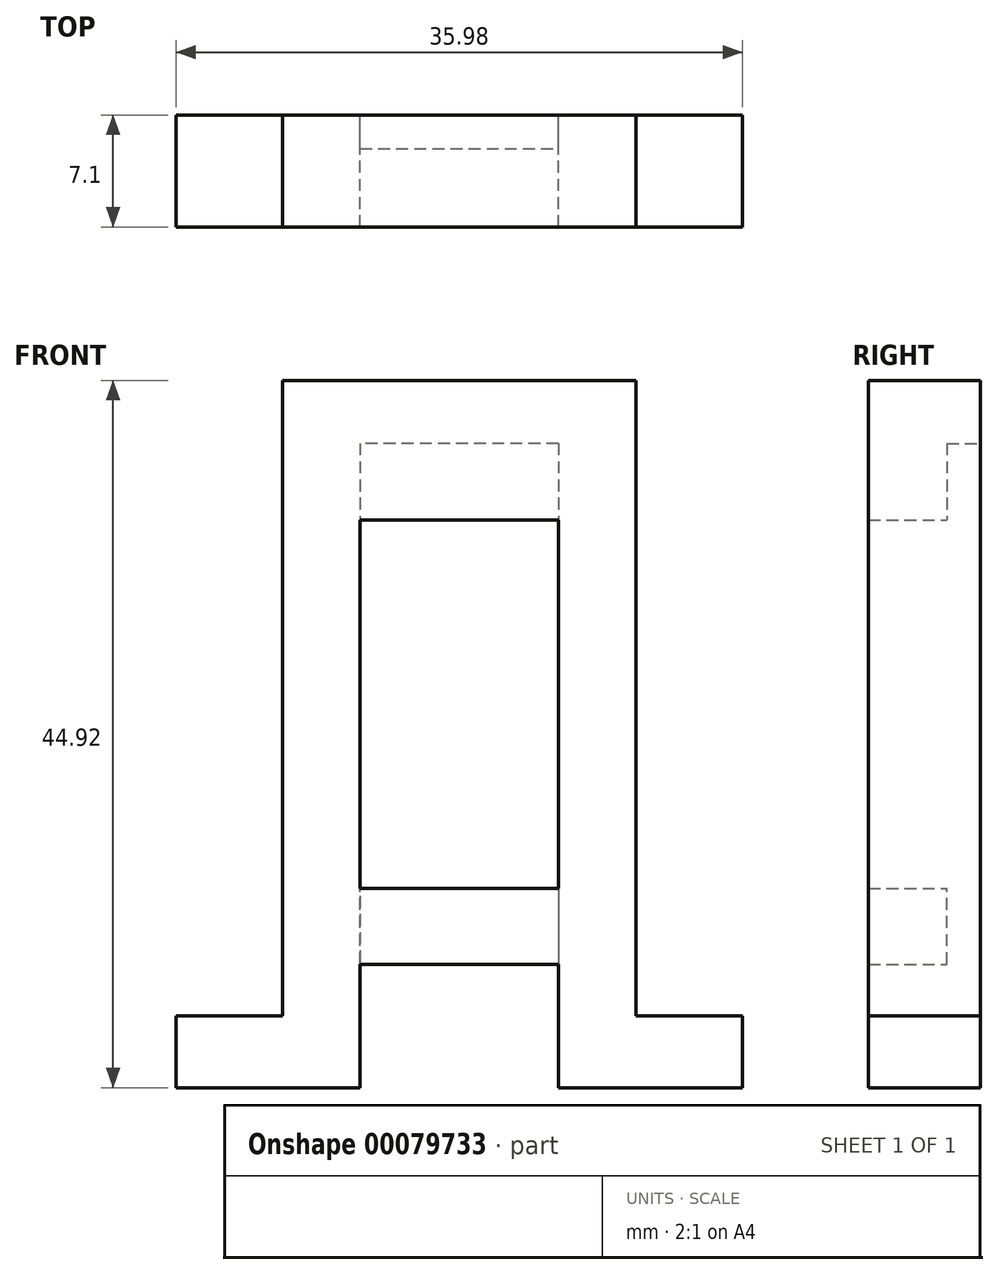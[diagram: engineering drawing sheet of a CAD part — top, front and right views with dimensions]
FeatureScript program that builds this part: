
annotation { "Feature Type Name" : "Feature", "Feature Type Description" : "" }
export const myFeature = defineFeature(function(context is Context, id is Id, definition is map)
    precondition{}
    {
        {
            var Q0;
            Q0=qCreatedBy(makeId("Front.planeOp"),FACE);
            var sketch = newSketch(context, id + "F0", { "sketchPlane" : qUnion([Q0])});
            skLineSegment(sketch, "E0.bottom", {"start": v(-11.23, 22.46) * mm, "end": v(11.23, 22.46) * mm});
            skLineSegment(sketch, "E0.top", {"start": v(-18, -22.46) * mm, "end": v(-6.3, -22.46) * mm});
            skLineSegment(sketch, "E0.left", {"start": v(-17.99, -17.91) * mm, "end": v(-17.99, -22.46) * mm});
            skLineSegment(sketch, "E0.right", {"start": v(17.99, -17.91) * mm, "end": v(17.99, -22.46) * mm});
            skPoint(sketch, "E0.middle", {"position": v(0, 0) * mm});
            skLineSegment(sketch, "E1", {"start": v(-18, -22.46) * mm, "end": v(-18, -17.91) * mm, "construction": true});
            skLineSegment(sketch, "E2", {"start": v(-18, -17.91) * mm, "end": v(-11.23, -17.91) * mm, "construction": true});
            skLineSegment(sketch, "E3", {"start": v(-18, -22.46) * mm, "end": v(-6.3, -22.46) * mm, "construction": true});
            skLineSegment(sketch, "E4", {"start": v(17.99, -22.46) * mm, "end": v(6.3, -22.46) * mm, "construction": true});
            skLineSegment(sketch, "E5", {"start": v(-6.3, -22.46) * mm, "end": v(-6.3, -14.62) * mm, "construction": true});
            skLineSegment(sketch, "E6", {"start": v(6.3, -22.46) * mm, "end": v(6.3, -14.62) * mm, "construction": true});
            skLineSegment(sketch, "E7", {"start": v(-6.3, 13.58) * mm, "end": v(6.3, 13.58) * mm, "construction": true});
            skLineSegment(sketch, "E8.trimOffspring", {"start": v(11.23, -17.91) * mm, "end": v(17.99, -17.91) * mm, "construction": true});
            skLineSegment(sketch, "E9", {"start": v(-6.3, 13.58) * mm, "end": v(-6.3, -9.82) * mm});
            skLineSegment(sketch, "E10", {"start": v(-6.3, 13.58) * mm, "end": v(6.3, 13.58) * mm});
            skLineSegment(sketch, "E11", {"start": v(-6.3, -9.82) * mm, "end": v(6.3, -9.82) * mm});
            skLineSegment(sketch, "E12", {"start": v(6.3, -9.82) * mm, "end": v(6.3, 13.58) * mm});
            skLineSegment(sketch, "E13", {"start": v(-6.3, -14.62) * mm, "end": v(6.3, -14.62) * mm});
            skLineSegment(sketch, "E14", {"start": v(6.3, -14.62) * mm, "end": v(6.3, -22.46) * mm});
            skLineSegment(sketch, "E15", {"start": v(-6.3, -14.62) * mm, "end": v(-6.3, -22.46) * mm});
            skLineSegment(sketch, "E16", {"start": v(-6.3, 22.46) * mm, "end": v(-11.23, 22.46) * mm, "construction": true});
            skLineSegment(sketch, "E17", {"start": v(6.3, 22.46) * mm, "end": v(11.23, 22.46) * mm, "construction": true});
            skLineSegment(sketch, "E18", {"start": v(-11.23, 22.46) * mm, "end": v(-11.23, -17.91) * mm});
            skLineSegment(sketch, "E19", {"start": v(-11.23, -17.91) * mm, "end": v(-18, -17.91) * mm});
            skLineSegment(sketch, "E20", {"start": v(11.23, 22.46) * mm, "end": v(11.23, -17.91) * mm});
            skLineSegment(sketch, "E21", {"start": v(11.23, -17.91) * mm, "end": v(17.99, -17.91) * mm});
            skLineSegment(sketch, "E22.trimOffspring", {"start": v(6.3, -22.46) * mm, "end": v(17.99, -22.46) * mm});
            skLineSegment(sketch, "E23.trimOffspring", {"start": v(6.3, -9.82) * mm, "end": v(6.3, 13.58) * mm, "construction": true});
            skLineSegment(sketch, "E24.trimOffspring", {"start": v(-6.3, -9.82) * mm, "end": v(-6.3, 13.58) * mm, "construction": true});
            skSolve(sketch);
        }
        {
            var Q0;
            Q0 = qSketchRegion(id + "F0", true);
            extrude(context, id + "F1", {"entities" : qUnion([Q0]), "depth" : 7.1 * mm});
        }
        {
            var Q0;
            Q0=makeQuery(id+"F1.opExtrude","CAP_FACE",FACE,{"disambiguationData":[OSD([sQuery(id+"F0.wireOp",EDGE,"E0.bottom"),sQuery(id+"F0.wireOp",EDGE,"E0.top"),sQuery(id+"F0.wireOp",EDGE,"E0.left"),sQuery(id+"F0.wireOp",EDGE,"E0.right"),sQuery(id+"F0.wireOp",EDGE,"E9"),sQuery(id+"F0.wireOp",EDGE,"E10"),sQuery(id+"F0.wireOp",EDGE,"E11"),sQuery(id+"F0.wireOp",EDGE,"E12"),sQuery(id+"F0.wireOp",EDGE,"E13"),sQuery(id+"F0.wireOp",EDGE,"E14"),sQuery(id+"F0.wireOp",EDGE,"E15"),sQuery(id+"F0.wireOp",EDGE,"E18"),sQuery(id+"F0.wireOp",EDGE,"E19"),sQuery(id+"F0.wireOp",EDGE,"E20"),sQuery(id+"F0.wireOp",EDGE,"E21"),sQuery(id+"F0.wireOp",EDGE,"E22.trimOffspring")])],"isStart":true});
            var sketch = newSketch(context, id + "F2", { "sketchPlane" : qUnion([Q0])});
            skLineSegment(sketch, "E25", {"start": v(-6.3, -9.82) * mm, "end": v(-6.3, -14.62) * mm});
            skLineSegment(sketch, "E26", {"start": v(-6.3, -14.62) * mm, "end": v(6.3, -14.62) * mm});
            skLineSegment(sketch, "E27", {"start": v(6.3, -14.62) * mm, "end": v(6.3, -9.82) * mm});
            skLineSegment(sketch, "E28", {"start": v(6.3, -9.82) * mm, "end": v(-6.3, -9.82) * mm});
            skLineSegment(sketch, "E29", {"start": v(-6.3, 13.58) * mm, "end": v(-6.3, 22.46) * mm, "construction": true});
            skLineSegment(sketch, "E30", {"start": v(6.3, 13.58) * mm, "end": v(6.3, 22.46) * mm, "construction": true});
            skLineSegment(sketch, "E31", {"start": v(-6.3, 22.46) * mm, "end": v(-6.3, 18.46) * mm, "construction": true});
            skLineSegment(sketch, "E32", {"start": v(-6.3, 18.46) * mm, "end": v(6.3, 18.46) * mm});
            skLineSegment(sketch, "E33", {"start": v(6.3, 18.46) * mm, "end": v(6.3, 13.58) * mm});
            skLineSegment(sketch, "E34", {"start": v(-6.3, 18.46) * mm, "end": v(-6.3, 13.58) * mm});
            skLineSegment(sketch, "E35", {"start": v(6.3, 13.58) * mm, "end": v(-6.3, 13.58) * mm});
            skSolve(sketch);
        }
        {
            var Q0;
            Q0 = qSketchRegion(id + "F2", true);
            extrude(context, id + "F3", {"entities" : qUnion([Q0]), "operationType" : NewBodyOperationType.REMOVE, "oppositeDirection" : true, "depth" : 2.12 * mm});
        }
    });
